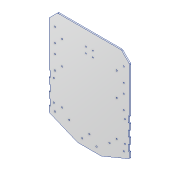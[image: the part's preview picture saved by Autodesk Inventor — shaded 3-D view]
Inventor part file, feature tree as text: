
AUTODESK INVENTOR PART (.ipt)
format: ipt  version: 2020 (Build 240168000, 168)  size: 413,184 bytes
history: native  units: mm
features: sketch x4, other x3, extrude x3
ambient origin geometry x8: Origin, YZ Plane, XZ Plane, XY Plane, X Axis, Y Axis, Z Axis, Center Point
bodies: Body1 (feature_tree)
feature tree (10):
  other  "솔리드1"
  extrude  "돌출1"  Depth=5.0mm
  other  "모서리 라운드1"
  extrude  "돌출2"  Depth=75.0mm
  extrude  "돌출3"  TaperAngle=0.0deg  [1 undecoded]
  sketch  "스케치1"
  sketch  "스케치2"
  sketch  "스케치3"
  sketch  "스케치5"
  other  "정의1"
note: 1 required parameter value undecoded (feature->parameter linkage not recoverable at this tier; creation-order binding heuristic only, values carry confidence <= 0.55)
